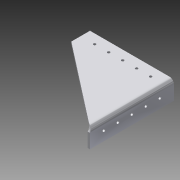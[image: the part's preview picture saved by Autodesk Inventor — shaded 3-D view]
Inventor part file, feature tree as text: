
AUTODESK INVENTOR PART (.ipt)
format: ipt  version: 2015 SP1 (Build 190203100, 203)  size: 160,256 bytes
history: native  units: in
note: dims shown in document units (in); Inventor stores cm internally (conversion verified against a paired STEP export)
features: other x5, sheet_metal_op x3, hole x2, sketch x2
ambient origin geometry x8: Origin, YZ Plane, XZ Plane, XY Plane, X Axis, Y Axis, Z Axis, Center Point
bodies: Solid1 (feature_tree)
feature tree (12):
  other  "<userpath>\Documents\2015 Offseason Chassis\West Coast Chassis Fall 2015\rivet(rv).xlsx"
  hole  "Hole1"  [1 undecoded]
  sheet_metal_op  "Flange1"
  hole  "Hole2"  [1 undecoded]
  other  "face_sketch"
  other  "Plate1"
  other  "crossbar_rivet_holes_sketch"
  sketch  "Sketch3"  dims[d0=1.0in d1=4.5in]
  other  "Plate2"
  sheet_metal_op  "Bend1"
  sheet_metal_op  "Corner1"
  sketch  "Sketch4"  dims[d2=4.5in d3=0.12in d4=0.1406in d5=0.75in d6=0.375in d7=0.25in d8=0.5635in d9=0.12in d10=0.8108in d11=0.12in d12=0.06in d13=0.24in d14=0.12in d15=1.0in d16=90.0deg d17=0.12in d18=0.48in d19=0.12in d20=0.12in d21=0.5in d22=0.1406in d23=0.75in d24=0.375in d25=0.25in d26=0.5635in d27=0.12in d28=0.8108in]
note: 2 required parameter values undecoded (feature->parameter linkage not recoverable at this tier; creation-order binding heuristic only, values carry confidence <= 0.55)
